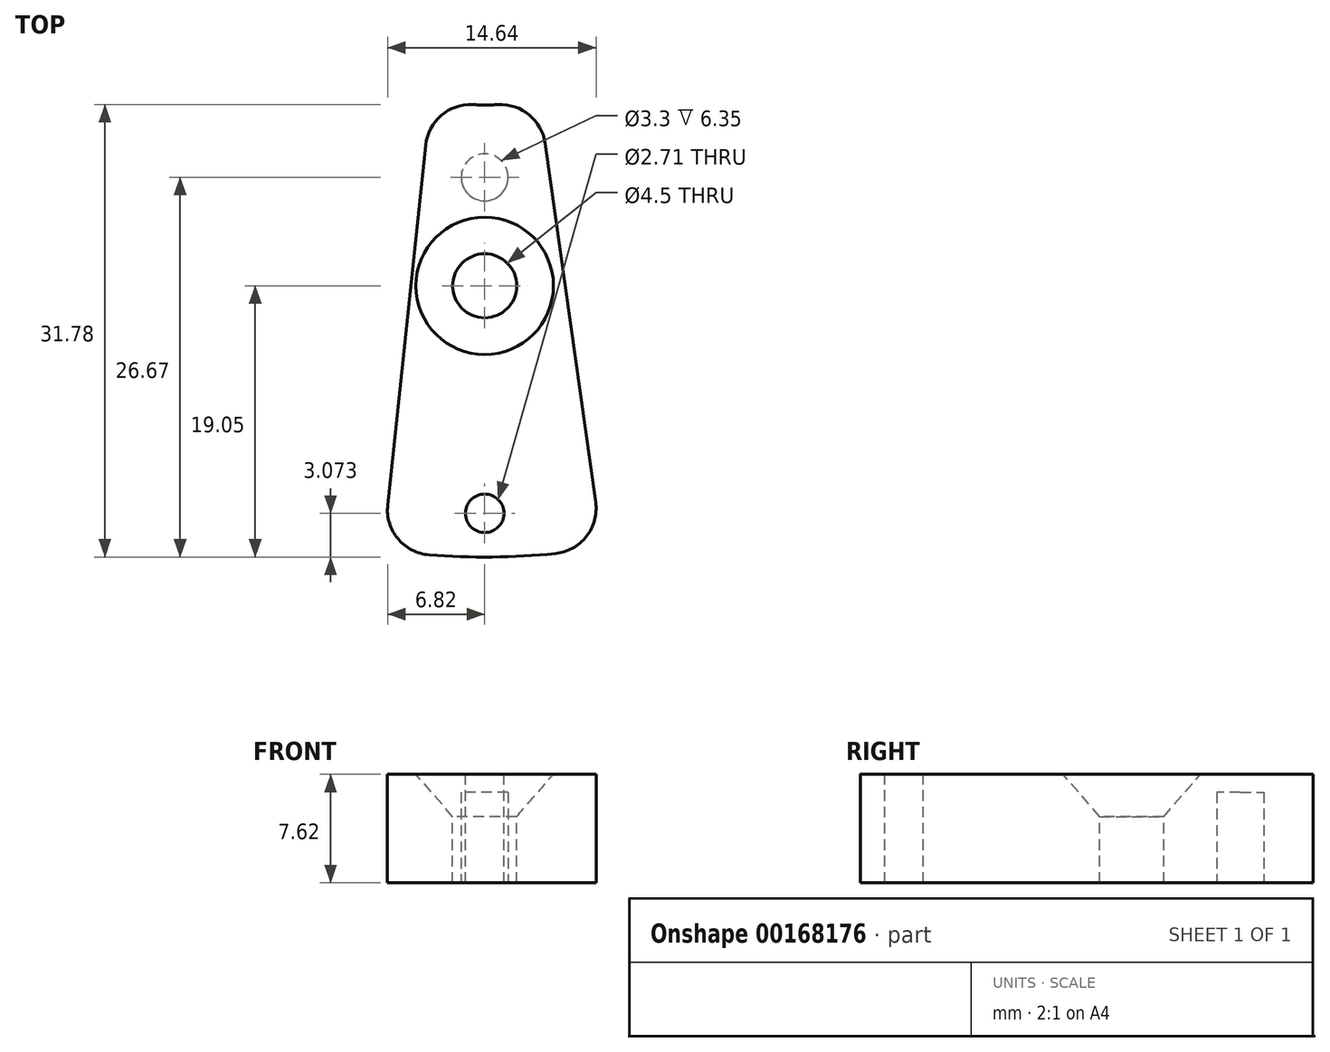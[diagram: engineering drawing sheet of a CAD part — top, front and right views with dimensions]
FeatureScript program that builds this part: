
annotation { "Feature Type Name" : "Feature", "Feature Type Description" : "" }
export const myFeature = defineFeature(function(context is Context, id is Id, definition is map)
    precondition{}
    {
        {
            var Q0;
            Q0=qCreatedBy(makeId("Top.planeOp"),FACE);
            var sketch = newSketch(context, id + "F0", { "sketchPlane" : qUnion([Q0])});
            skArc(sketch, "E0", {"start": v(3.81, -17.37) * mm, "mid": v(0, -17.78) * mm, "end": v(-3.81, -17.37) * mm});
            skArc(sketch, "E1", {"start": v(8.23, -48.84) * mm, "mid": v(0.56, -49.53) * mm, "end": v(-7.14, -49.01) * mm});
            skLineSegment(sketch, "E2", {"start": v(-3.81, -17.37) * mm, "end": v(3.81, -17.37) * mm, "construction": true});
            skLineSegment(sketch, "E3", {"start": v(0, 0) * mm, "end": v(-3.81, -17.37) * mm, "construction": true});
            skLineSegment(sketch, "E4", {"start": v(0, 0) * mm, "end": v(3.81, -17.37) * mm, "construction": true});
            skLineSegment(sketch, "E5", {"start": v(-3.81, -17.37) * mm, "end": v(-7.14, -49.01) * mm});
            skLineSegment(sketch, "E6", {"start": v(3.81, -17.37) * mm, "end": v(8.23, -48.84) * mm});
            skPoint(sketch, "E7", {"position": v(0, -17.37) * mm});
            skSolve(sketch);
        }
        {
            var Q0;
            Q0=qSketchRegion(id+"F0",true);
            extrude(context, id + "F1", {"entities" : qUnion([Q0]), "depth" : 7.62 * mm});
        }
        {
            var Q0;
            Q0=makeQuery(id+"F1.opExtrude","SWEPT_EDGE",EDGE,{"disambiguationData":[OSD([sQuery(id+"F0.wireOp",EDGE,"E1"),sQuery(id+"F0.wireOp",EDGE,"E5")])]});
            var Q1;
            Q1=makeQuery(id+"F1.opExtrude","SWEPT_EDGE",EDGE,{"disambiguationData":[OSD([sQuery(id+"F0.wireOp",EDGE,"E0"),sQuery(id+"F0.wireOp",EDGE,"E5")])]});
            var Q2;
            Q2=makeQuery(id+"F1.opExtrude","SWEPT_EDGE",EDGE,{"disambiguationData":[OSD([sQuery(id+"F0.wireOp",EDGE,"E1"),sQuery(id+"F0.wireOp",EDGE,"E6")])]});
            var Q3;
            Q3=makeQuery(id+"F1.opExtrude","SWEPT_EDGE",EDGE,{"disambiguationData":[OSD([sQuery(id+"F0.wireOp",EDGE,"E0"),sQuery(id+"F0.wireOp",EDGE,"E6")])]});
            fillet(context, id + "F2", {"entities" : qUnion([Q0, Q1, Q2, Q3]), "radius" : 3.17 * mm, "tangentPropagation" : true, "allowEdgeOverflow" : false});
        }
        {
            var Q0;
            Q0=makeQuery(id+"F1.opExtrude","CAP_FACE",FACE,{"disambiguationData":[OSD([sQuery(id+"F0.wireOp",EDGE,"E0"),sQuery(id+"F0.wireOp",EDGE,"E1"),sQuery(id+"F0.wireOp",EDGE,"E5"),sQuery(id+"F0.wireOp",EDGE,"E6")])],"isStart":false});
            var sketch = newSketch(context, id + "F3", { "sketchPlane" : qUnion([Q0])});
            skPoint(sketch, "E8", {"position": v(0, -46.46) * mm});
            skSolve(sketch);
        }
        {
            var Q0;
            Q0=sQuery(id+"F3.wireOp",VERTEX,"E8");
            var Q1;
            Q1=makeQuery(id+"F1.opExtrude","SWEPT_BODY",BODY,{"disambiguationData":[OSD([sQuery(id+"F0.wireOp",EDGE,"E0"),sQuery(id+"F0.wireOp",EDGE,"E1"),sQuery(id+"F0.wireOp",EDGE,"E5"),sQuery(id+"F0.wireOp",EDGE,"E6")])]});
            hole(context, id + "F4", {"style" : HoleStyle.SIMPLE, "endStyle" : HoleEndStyle.THROUGH, "standardTappedOrClearance" : lookupTablePath({ "standard" : "ANSI", "engagement" : "75%", "pitch" : "32 tpi", "size" : "#6", "type" : "Tapped" }), "standardBlindInLast" : lookupTablePath({ "standard" : "ANSI", "engagement" : "75%", "pitch" : "32 tpi", "size" : "#6", "type" : "Tapped" }), "holeDiameter" : 2.7 * mm, "locations" : qUnion([Q0]), "scope" : qUnion([Q1]), "isTappedThrough" : true, "majorDiameter" : 3.5 * mm, "showTappedDepth" : true});
        }
        {
            var Q0;
            Q0=makeQuery(id+"F1.opExtrude","CAP_FACE",FACE,{"disambiguationData":[OSD([sQuery(id+"F0.wireOp",EDGE,"E0"),sQuery(id+"F0.wireOp",EDGE,"E1"),sQuery(id+"F0.wireOp",EDGE,"E5"),sQuery(id+"F0.wireOp",EDGE,"E6")])],"isStart":false});
            var sketch = newSketch(context, id + "F5", { "sketchPlane" : qUnion([Q0])});
            skPoint(sketch, "E9", {"position": v(0, -30.48) * mm});
            skSolve(sketch);
        }
        {
            var Q0;
            Q0=sQuery(id+"F5.wireOp",VERTEX,"E9");
            var Q1;
            Q1=makeQuery(id+"F1.opExtrude","SWEPT_BODY",BODY,{"disambiguationData":[OSD([sQuery(id+"F0.wireOp",EDGE,"E0"),sQuery(id+"F0.wireOp",EDGE,"E1"),sQuery(id+"F0.wireOp",EDGE,"E5"),sQuery(id+"F0.wireOp",EDGE,"E6")])]});
            hole(context, id + "F6", {"style" : HoleStyle.C_SINK, "endStyle" : HoleEndStyle.THROUGH, "holeDiameter" : 4.5 * mm, "cSinkDiameter" : 9.65 * mm, "cSinkAngle" : 82 * degree, "locations" : qUnion([Q0]), "scope" : qUnion([Q1]), "isTappedThrough" : true});
        }
        {
            var Q0;
            Q0=makeQuery(id+"F1.opExtrude","CAP_FACE",FACE,{"disambiguationData":[OSD([sQuery(id+"F0.wireOp",EDGE,"E0"),sQuery(id+"F0.wireOp",EDGE,"E1"),sQuery(id+"F0.wireOp",EDGE,"E5"),sQuery(id+"F0.wireOp",EDGE,"E6")])],"isStart":true});
            var sketch = newSketch(context, id + "F7", { "sketchPlane" : qUnion([Q0])});
            skCircle(sketch, "E10", {"center": v(0, 22.86) * mm, "radius": 1.65 * mm});
            skSolve(sketch);
        }
        {
            var Q0;
            Q0=qSketchRegion(id+"F7",true);
            extrude(context, id + "F8", {"entities" : qUnion([Q0]), "operationType" : NewBodyOperationType.REMOVE, "endBound" : BoundingType.THROUGH_ALL, "oppositeDirection" : true, "depth" : 25.4 * mm});
        }
        {
            var Q0;
            Q0=makeQuery(id+"F1.opExtrude","CAP_FACE",FACE,{"disambiguationData":[OSD([sQuery(id+"F0.wireOp",EDGE,"E0"),sQuery(id+"F0.wireOp",EDGE,"E1"),sQuery(id+"F0.wireOp",EDGE,"E5"),sQuery(id+"F0.wireOp",EDGE,"E6")])],"isStart":false});
            var sketch = newSketch(context, id + "F9", { "sketchPlane" : qUnion([Q0])});
            skCircle(sketch, "E11.0", {"center": v(0, -22.86) * mm, "radius": 1.65 * mm});
            skSolve(sketch);
        }
        {
            var Q0;
            Q0=qSketchRegion(id+"F9",true);
            extrude(context, id + "F10", {"entities" : qUnion([Q0]), "operationType" : NewBodyOperationType.ADD, "oppositeDirection" : true, "depth" : 1.27 * mm});
        }
    });
